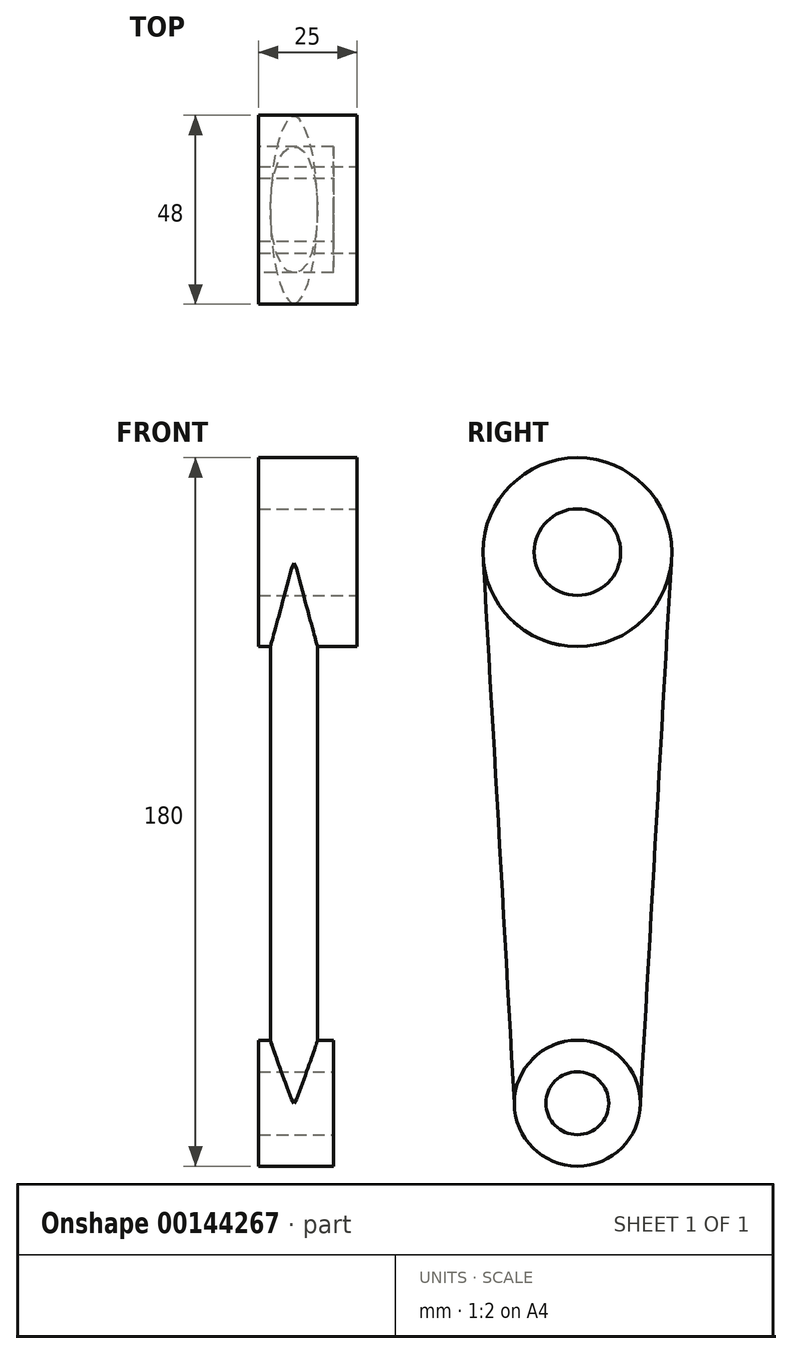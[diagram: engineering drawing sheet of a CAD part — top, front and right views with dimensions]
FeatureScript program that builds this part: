
annotation { "Feature Type Name" : "Feature", "Feature Type Description" : "" }
export const myFeature = defineFeature(function(context is Context, id is Id, definition is map)
    precondition{}
    {
        {
            var Q0;
            Q0=qCreatedBy(makeId("Right.planeOp"),FACE);
            var sketch = newSketch(context, id + "F0", { "sketchPlane" : qUnion([Q0])});
            skCircle(sketch, "E0", {"center": v(0, 0) * mm, "radius": 16 * mm});
            skCircle(sketch, "E1", {"center": v(0, 0) * mm, "radius": 8 * mm});
            skCircle(sketch, "E2", {"center": v(0, 140) * mm, "radius": 24 * mm});
            skCircle(sketch, "E3", {"center": v(0, 140) * mm, "radius": 11 * mm});
            skSolve(sketch);
        }
        {
            var Q0;
            Q0=makeQuery(id+"F0.imprint","IMPRINT",FACE,{"disambiguationData":[TD([[makeQuery(id+"F0.imprint","IMPRINT",EDGE,{"derivedFrom":sQuery(id+"F0.wireOp",EDGE,"E1")}),1.0]])]});
            var Q1;
            Q1=makeQuery(id+"F0.imprint","IMPRINT",FACE,{"disambiguationData":[TD([[makeQuery(id+"F0.imprint","IMPRINT",EDGE,{"derivedFrom":sQuery(id+"F0.wireOp",EDGE,"E0")}),1.0]])]});
            extrude(context, id + "F1", {"entities" : qUnion([Q0, Q1]), "depth" : 19 * mm});
        }
        {
            var Q0;
            Q0=makeQuery(id+"F0.imprint","IMPRINT",FACE,{"disambiguationData":[TD([[makeQuery(id+"F0.imprint","IMPRINT",EDGE,{"derivedFrom":sQuery(id+"F0.wireOp",EDGE,"E2")}),1.0]])]});
            extrude(context, id + "F2", {"entities" : qUnion([Q0]), "depth" : 25 * mm});
        }
        {
            var Q0;
            Q0=qCreatedBy(makeId("Top.planeOp"),FACE);
            var sketch = newSketch(context, id + "F3", { "sketchPlane" : qUnion([Q0])});
            skEllipse(sketch, "E4", {"center": v(9, 0) * mm, "majorRadius": 16 * mm, "minorRadius": 6 * mm, "majorAxis": v(0, -1)});
            skPoint(sketch, "E5", {"position": v(3, 0) * mm});
            skLineSegment(sketch, "E6", {"start": v(0, 16) * mm, "end": v(19, 16) * mm, "construction": true});
            skSolve(sketch);
        }
        {
            var Q0;
            Q0=makeQuery(id+"F2.opExtrude","CAP_FACE",FACE,{"disambiguationData":[OSD([sQuery(id+"F0.wireOp",EDGE,"E2"),sQuery(id+"F0.wireOp",EDGE,"E3")])],"isStart":false});
            var sketch = newSketch(context, id + "F4", { "sketchPlane" : qUnion([Q0])});
            skCircle(sketch, "E7", {"center": v(0, 140) * mm, "radius": 11 * mm});
            skSolve(sketch);
        }
        {
            var Q0;
            Q0=makeQuery(id+"F4.imprint","IMPRINT",FACE,{"disambiguationData":[TD([[makeQuery(id+"F4.imprint","IMPRINT",EDGE,{"derivedFrom":sQuery(id+"F4.wireOp",EDGE,"E7")}),1.0]])]});
            extrude(context, id + "F5", {"entities" : qUnion([Q0]), "oppositeDirection" : true, "depth" : 25 * mm});
        }
        {
            var Q0;
            Q0=makeQuery(id+"F5.opExtrude","CAP_FACE",FACE,{"disambiguationData":[OSD([sQuery(id+"F4.wireOp",EDGE,"E7")])],"isStart":true});
            var sketch = newSketch(context, id + "F6", { "sketchPlane" : qUnion([Q0])});
            skPoint(sketch, "E8", {"position": v(0, 140) * mm});
            skSolve(sketch);
        }
        {
            var Q0;
            Q0=sQuery(id+"F6.wireOp",VERTEX,"E8");
            var Q1;
            Q1=qCreatedBy(makeId("Top.planeOp"),FACE);
            cPlane(context, id + "F7", {"entities" : qUnion([Q0, Q1]), "cplaneType" : CPlaneType.PLANE_POINT, "offset" : 25 * mm, "width" : 150 * mm, "height" : 150 * mm});
        }
        {
            var Q0;
            Q0=qCreatedBy(id+"F7.planeOp",FACE);
            var sketch = newSketch(context, id + "F8", { "sketchPlane" : qUnion([Q0])});
            skEllipse(sketch, "E9", {"center": v(9, 0) * mm, "majorRadius": 24 * mm, "minorRadius": 6 * mm, "majorAxis": v(0, -1)});
            skPoint(sketch, "E10", {"position": v(3, 0) * mm});
            skLineSegment(sketch, "E11", {"start": v(0, 24) * mm, "end": v(25, 24) * mm, "construction": true});
            skSolve(sketch);
        }
        {
            var Q0;
            Q0=makeQuery(id+"F8.imprint","IMPRINT",FACE,{"disambiguationData":[TD([[makeQuery(id+"F8.imprint","IMPRINT",EDGE,{"derivedFrom":sQuery(id+"F8.wireOp",EDGE,"E9")}),1.0]])]});
            var Q1;
            Q1=makeQuery(id+"F3.imprint","IMPRINT",FACE,{"disambiguationData":[TD([[makeQuery(id+"F3.imprint","IMPRINT",EDGE,{"derivedFrom":sQuery(id+"F3.wireOp",EDGE,"E4")}),1.0]])]});
            loft(context, id + "F9", {"operationType" : NewBodyOperationType.ADD, "sheetProfilesArray" : [{ "sheetProfileEntities" : qUnion([Q0]) }, { "sheetProfileEntities" : qUnion([Q1]) }]});
        }
        {
            var Q0;
            Q0=makeQuery(id+"F6.imprint","IMPRINT",FACE,{"disambiguationData":[TD([[makeQuery(id+"F6.imprint","IMPRINT",EDGE,{"derivedFrom":makeQuery(id+"F5.opExtrude","CAP_EDGE",EDGE,{"disambiguationData":[OSD([sQuery(id+"F4.wireOp",EDGE,"E7")])],"isStart":true})}),1.0]])]});
            extrude(context, id + "F10", {"entities" : qUnion([Q0]), "operationType" : NewBodyOperationType.REMOVE, "endBound" : BoundingType.THROUGH_ALL, "oppositeDirection" : true, "depth" : 25 * mm});
        }
        {
            var Q0;
            Q0=makeQuery(id+"F1.opExtrude","CAP_FACE",FACE,{"disambiguationData":[OSD([sQuery(id+"F0.wireOp",EDGE,"E0")])],"isStart":false});
            var sketch = newSketch(context, id + "F11", { "sketchPlane" : qUnion([Q0])});
            skCircle(sketch, "E12", {"center": v(0, 0) * mm, "radius": 8 * mm});
            skSolve(sketch);
        }
        {
            var Q0;
            Q0=makeQuery(id+"F11.imprint","IMPRINT",FACE,{"disambiguationData":[TD([[makeQuery(id+"F11.imprint","IMPRINT",EDGE,{"derivedFrom":sQuery(id+"F11.wireOp",EDGE,"E12")}),1.0]])]});
            extrude(context, id + "F12", {"entities" : qUnion([Q0]), "operationType" : NewBodyOperationType.REMOVE, "endBound" : BoundingType.THROUGH_ALL, "oppositeDirection" : true, "depth" : 25 * mm});
        }
    });
